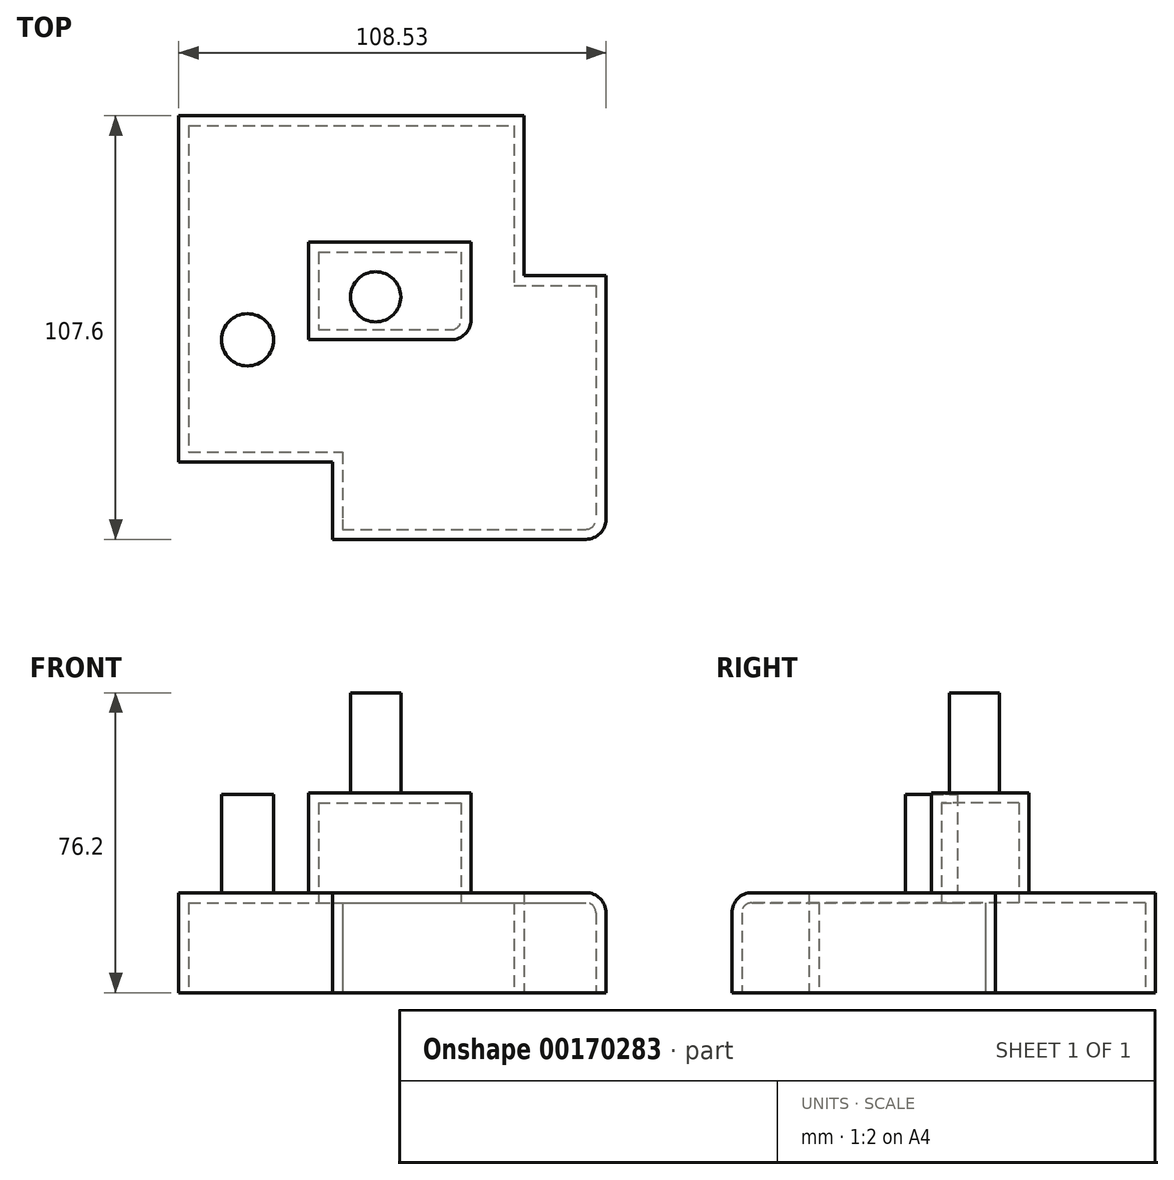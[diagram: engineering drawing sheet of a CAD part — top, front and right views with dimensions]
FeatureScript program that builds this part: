
annotation { "Feature Type Name" : "Feature", "Feature Type Description" : "" }
export const myFeature = defineFeature(function(context is Context, id is Id, definition is map)
    precondition{}
    {
        {
            var Q0;
            Q0=qCreatedBy(makeId("Top.planeOp"),FACE);
            var sketch = newSketch(context, id + "F0", { "sketchPlane" : qUnion([Q0])});
            skLineSegment(sketch, "E0.bottom", {"start": v(-58.88, 56.92) * mm, "end": v(28.86, 56.92) * mm});
            skLineSegment(sketch, "E0.top", {"start": v(-58.88, -31.06) * mm, "end": v(-19.86, -31.06) * mm});
            skLineSegment(sketch, "E0.left", {"start": v(-58.88, 56.92) * mm, "end": v(-58.88, -31.06) * mm});
            skLineSegment(sketch, "E0.right", {"start": v(28.86, 56.92) * mm, "end": v(28.86, 16.28) * mm});
            skLineSegment(sketch, "E1.bottom", {"start": v(28.86, 16.28) * mm, "end": v(49.65, 16.28) * mm});
            skLineSegment(sketch, "E1.top", {"start": v(-19.86, -50.68) * mm, "end": v(49.65, -50.68) * mm});
            skLineSegment(sketch, "E1.left", {"start": v(-19.86, -31.06) * mm, "end": v(-19.86, -50.68) * mm});
            skLineSegment(sketch, "E1.right", {"start": v(49.65, 16.28) * mm, "end": v(49.65, -50.68) * mm});
            skSolve(sketch);
        }
        {
            var Q0;
            Q0=makeQuery(id+"F0.imprint","IMPRINT",FACE,{"disambiguationData":[TD([[makeQuery(id+"F0.imprint","IMPRINT",EDGE,{"derivedFrom":sQuery(id+"F0.wireOp",EDGE,"E0.bottom")}),-1.0]])]});
            extrude(context, id + "F1", {"entities" : qUnion([Q0]), "depth" : 25.4 * mm});
        }
        {
            var Q0;
            Q0=makeQuery(id+"F1.opExtrude","CAP_EDGE",EDGE,{"disambiguationData":[OSD([sQuery(id+"F0.wireOp",EDGE,"E1.top")])],"isStart":false});
            fillet(context, id + "F2", {"entities" : qUnion([Q0]), "radius" : 5.08 * mm, "tangentPropagation" : true, "allowEdgeOverflow" : false});
        }
        {
            var Q0;
            Q0=makeQuery(id+"F1.opExtrude","CAP_EDGE",EDGE,{"disambiguationData":[OSD([sQuery(id+"F0.wireOp",EDGE,"E1.right")])],"isStart":false});
            fillet(context, id + "F3", {"entities" : qUnion([Q0]), "radius" : 5.08 * mm, "tangentPropagation" : true, "allowEdgeOverflow" : false});
        }
        {
            var Q0;
            Q0=makeQuery(id+"F1.opExtrude","CAP_FACE",FACE,{"disambiguationData":[OSD([sQuery(id+"F0.wireOp",EDGE,"E0.bottom"),sQuery(id+"F0.wireOp",EDGE,"E0.top"),sQuery(id+"F0.wireOp",EDGE,"E0.left"),sQuery(id+"F0.wireOp",EDGE,"E0.right"),sQuery(id+"F0.wireOp",EDGE,"E1.bottom"),sQuery(id+"F0.wireOp",EDGE,"E1.top"),sQuery(id+"F0.wireOp",EDGE,"E1.left"),sQuery(id+"F0.wireOp",EDGE,"E1.right")])],"isStart":false});
            var sketch = newSketch(context, id + "F4", { "sketchPlane" : qUnion([Q0])});
            skLineSegment(sketch, "E2.bottom", {"start": v(-25.97, 24.8) * mm, "end": v(15.37, 24.8) * mm});
            skLineSegment(sketch, "E2.top", {"start": v(-25.97, 0) * mm, "end": v(15.37, 0) * mm});
            skLineSegment(sketch, "E2.left", {"start": v(-25.97, 24.8) * mm, "end": v(-25.97, 0) * mm});
            skLineSegment(sketch, "E2.right", {"start": v(15.37, 24.8) * mm, "end": v(15.37, 0) * mm});
            skSolve(sketch);
        }
        {
            var Q0;
            Q0=makeQuery(id+"F4.imprint","IMPRINT",FACE,{"disambiguationData":[TD([[makeQuery(id+"F4.imprint","IMPRINT",EDGE,{"derivedFrom":sQuery(id+"F4.wireOp",EDGE,"E2.bottom")}),-1.0]])]});
            extrude(context, id + "F5", {"entities" : qUnion([Q0]), "operationType" : NewBodyOperationType.ADD, "depth" : 25.4 * mm});
        }
        {
            var Q0;
            Q0=makeQuery(id+"F5.opExtrude","SWEPT_EDGE",EDGE,{"disambiguationData":[OSD([sQuery(id+"F4.wireOp",EDGE,"E2.top"),sQuery(id+"F4.wireOp",EDGE,"E2.right")])]});
            fillet(context, id + "F6", {"entities" : qUnion([Q0]), "radius" : 5.08 * mm, "tangentPropagation" : true, "allowEdgeOverflow" : false});
        }
        {
            var Q0;
            Q0=makeQuery(id+"F1.opExtrude","CAP_FACE",FACE,{"disambiguationData":[OSD([sQuery(id+"F0.wireOp",EDGE,"E0.bottom"),sQuery(id+"F0.wireOp",EDGE,"E0.top"),sQuery(id+"F0.wireOp",EDGE,"E0.left"),sQuery(id+"F0.wireOp",EDGE,"E0.right"),sQuery(id+"F0.wireOp",EDGE,"E1.bottom"),sQuery(id+"F0.wireOp",EDGE,"E1.top"),sQuery(id+"F0.wireOp",EDGE,"E1.left"),sQuery(id+"F0.wireOp",EDGE,"E1.right")])],"isStart":true});
            shell(context, id + "F7", {"entities" : qUnion([Q0]), "thickness" : 2.54 * mm});
        }
        {
            var Q0;
            Q0=makeQuery(id+"F5.opExtrude","CAP_FACE",FACE,{"disambiguationData":[OSD([sQuery(id+"F4.wireOp",EDGE,"E2.bottom"),sQuery(id+"F4.wireOp",EDGE,"E2.top"),sQuery(id+"F4.wireOp",EDGE,"E2.left"),sQuery(id+"F4.wireOp",EDGE,"E2.right")])],"isStart":false});
            var sketch = newSketch(context, id + "F8", { "sketchPlane" : qUnion([Q0])});
            skCircle(sketch, "E3", {"center": v(-8.84, 10.92) * mm, "radius": 6.37 * mm});
            skSolve(sketch);
        }
        {
            var Q0;
            Q0=makeQuery(id+"F8.imprint","IMPRINT",FACE,{"disambiguationData":[TD([[makeQuery(id+"F8.imprint","IMPRINT",EDGE,{"derivedFrom":sQuery(id+"F8.wireOp",EDGE,"E3")}),1.0]])]});
            extrude(context, id + "F9", {"entities" : qUnion([Q0]), "operationType" : NewBodyOperationType.ADD, "depth" : 25.4 * mm});
        }
        {
            var Q0;
            Q0=makeQuery(id+"F1.opExtrude","CAP_FACE",FACE,{"disambiguationData":[OSD([sQuery(id+"F0.wireOp",EDGE,"E0.bottom"),sQuery(id+"F0.wireOp",EDGE,"E0.top"),sQuery(id+"F0.wireOp",EDGE,"E0.left"),sQuery(id+"F0.wireOp",EDGE,"E0.right"),sQuery(id+"F0.wireOp",EDGE,"E1.bottom"),sQuery(id+"F0.wireOp",EDGE,"E1.top"),sQuery(id+"F0.wireOp",EDGE,"E1.left"),sQuery(id+"F0.wireOp",EDGE,"E1.right")])],"isStart":false});
            var sketch = newSketch(context, id + "F10", { "sketchPlane" : qUnion([Q0])});
            skCircle(sketch, "E4", {"center": v(-41.42, 0) * mm, "radius": 6.62 * mm});
            skSolve(sketch);
        }
        {
            var Q0;
            Q0=makeQuery(id+"F10.imprint","IMPRINT",FACE,{"disambiguationData":[TD([[makeQuery(id+"F10.imprint","IMPRINT",EDGE,{"derivedFrom":sQuery(id+"F10.wireOp",EDGE,"E4")}),1.0]])]});
            extrude(context, id + "F11", {"entities" : qUnion([Q0]), "operationType" : NewBodyOperationType.ADD, "depth" : 25 * mm});
        }
    });
